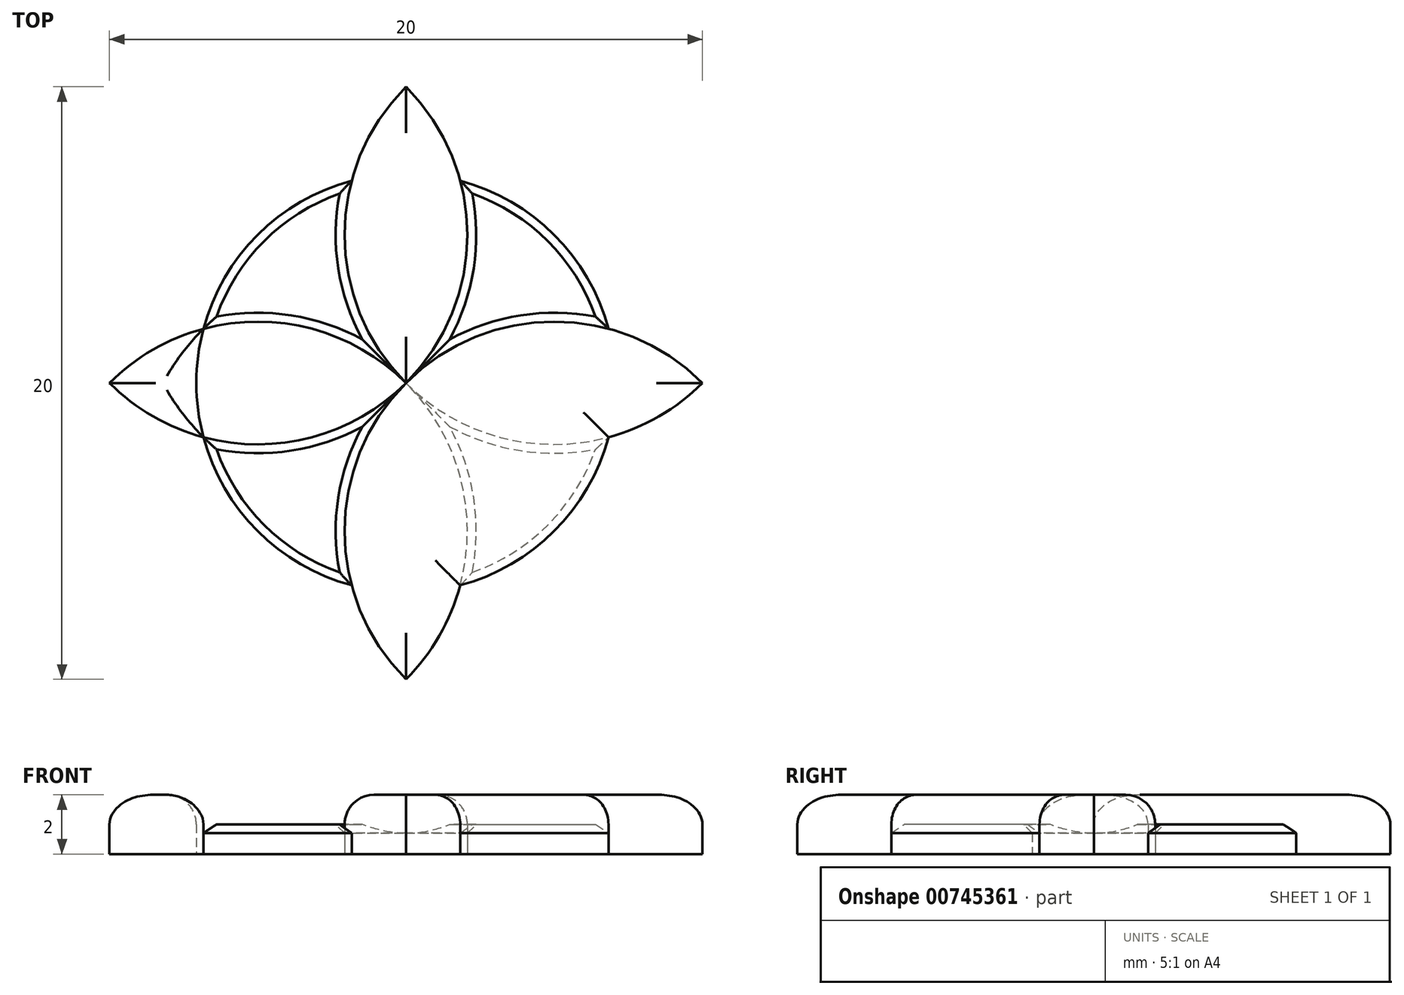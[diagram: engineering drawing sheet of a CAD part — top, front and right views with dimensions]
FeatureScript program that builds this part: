
annotation { "Feature Type Name" : "Feature", "Feature Type Description" : "" }
export const myFeature = defineFeature(function(context is Context, id is Id, definition is map)
    precondition{}
    {
        {
            var Q0;
            Q0=qCreatedBy(makeId("Top.planeOp"),FACE);
            var sketch = newSketch(context, id + "F0", { "sketchPlane" : qUnion([Q0])});
            skPoint(sketch, "E0.middle", {"position": v(0, 0) * mm});
            skArc(sketch, "E1", {"start": v(0, 10) * mm, "mid": v(0, 0) * mm, "end": v(10, 0) * mm});
            skArc(sketch, "E2", {"start": v(10, 0) * mm, "mid": v(0, 0) * mm, "end": v(0, -10) * mm});
            skArc(sketch, "E3", {"start": v(0, -10) * mm, "mid": v(0, 0) * mm, "end": v(-10, 0) * mm});
            skArc(sketch, "E4", {"start": v(-10, 0) * mm, "mid": v(0, 0) * mm, "end": v(0, 10) * mm});
            skCircle(sketch, "E5", {"center": v(0, 0) * mm, "radius": 7.07 * mm});
            skSolve(sketch);
        }
        {
            var Q0;
            {var subQ0=sQuery(id+"F0.wireOp",EDGE,"E5");var subQ1=sQuery(id+"F0.wireOp",EDGE,"E1");var subQ2=makeQuery(id+"F0.imprint","INTERSECT",VERTEX,{"disambiguationData":[OD(0.0)],"derivedFrom":[subQ1,subQ0]});Q0=makeQuery(id+"F0.imprint","IMPRINT",FACE,{"disambiguationData":[TD([[makeQuery(id+"F0.imprint","IMPRINT",EDGE,{"disambiguationData":[TD([[subQ2,1.0]])],"derivedFrom":subQ0}),1.0]])]});}
            var Q1;
            {var subQ0=sQuery(id+"F0.wireOp",EDGE,"E4");var subQ1=sQuery(id+"F0.wireOp",EDGE,"E1");var subQ2=makeQuery(id+"F0.imprint","INTERSECT",VERTEX,{"derivedFrom":[subQ1,subQ0]});Q1=makeQuery(id+"F0.imprint","IMPRINT",FACE,{"disambiguationData":[TD([[makeQuery(id+"F0.imprint","IMPRINT",EDGE,{"disambiguationData":[TD([[subQ2,-1.0]])],"derivedFrom":subQ1}),1.0]])]});}
            var Q2;
            {var subQ0=sQuery(id+"F0.wireOp",EDGE,"E5");var subQ1=sQuery(id+"F0.wireOp",EDGE,"E1");var subQ2=makeQuery(id+"F0.imprint","INTERSECT",VERTEX,{"disambiguationData":[OD(1.0)],"derivedFrom":[subQ1,subQ0]});Q2=makeQuery(id+"F0.imprint","IMPRINT",FACE,{"disambiguationData":[TD([[makeQuery(id+"F0.imprint","IMPRINT",EDGE,{"disambiguationData":[TD([[subQ2,-1.0]])],"derivedFrom":subQ0}),1.0]])]});}
            var Q3;
            {var subQ0=sQuery(id+"F0.wireOp",EDGE,"E2");var subQ1=sQuery(id+"F0.wireOp",EDGE,"E1");var subQ2=makeQuery(id+"F0.imprint","INTERSECT",VERTEX,{"derivedFrom":[subQ1,subQ0]});Q3=makeQuery(id+"F0.imprint","IMPRINT",FACE,{"disambiguationData":[TD([[makeQuery(id+"F0.imprint","IMPRINT",EDGE,{"disambiguationData":[TD([[subQ2,1.0]])],"derivedFrom":subQ1}),1.0]])]});}
            var Q4;
            {var subQ0=sQuery(id+"F0.wireOp",EDGE,"E5");var subQ1=sQuery(id+"F0.wireOp",EDGE,"E2");var subQ2=makeQuery(id+"F0.imprint","INTERSECT",VERTEX,{"disambiguationData":[OD(1.0)],"derivedFrom":[subQ1,subQ0]});Q4=makeQuery(id+"F0.imprint","IMPRINT",FACE,{"disambiguationData":[TD([[makeQuery(id+"F0.imprint","IMPRINT",EDGE,{"disambiguationData":[TD([[subQ2,-1.0]])],"derivedFrom":subQ0}),1.0]])]});}
            var Q5;
            {var subQ0=sQuery(id+"F0.wireOp",EDGE,"E3");var subQ1=sQuery(id+"F0.wireOp",EDGE,"E2");var subQ2=makeQuery(id+"F0.imprint","INTERSECT",VERTEX,{"derivedFrom":[subQ1,subQ0]});Q5=makeQuery(id+"F0.imprint","IMPRINT",FACE,{"disambiguationData":[TD([[makeQuery(id+"F0.imprint","IMPRINT",EDGE,{"disambiguationData":[TD([[subQ2,1.0]])],"derivedFrom":subQ1}),1.0]])]});}
            var Q6;
            {var subQ0=sQuery(id+"F0.wireOp",EDGE,"E5");var subQ1=sQuery(id+"F0.wireOp",EDGE,"E3");var subQ2=makeQuery(id+"F0.imprint","INTERSECT",VERTEX,{"disambiguationData":[OD(1.0)],"derivedFrom":[subQ1,subQ0]});Q6=makeQuery(id+"F0.imprint","IMPRINT",FACE,{"disambiguationData":[TD([[makeQuery(id+"F0.imprint","IMPRINT",EDGE,{"disambiguationData":[TD([[subQ2,-1.0]])],"derivedFrom":subQ0}),1.0]])]});}
            var Q7;
            {var subQ0=sQuery(id+"F0.wireOp",EDGE,"E4");var subQ1=sQuery(id+"F0.wireOp",EDGE,"E3");var subQ2=makeQuery(id+"F0.imprint","INTERSECT",VERTEX,{"derivedFrom":[subQ1,subQ0]});Q7=makeQuery(id+"F0.imprint","IMPRINT",FACE,{"disambiguationData":[TD([[makeQuery(id+"F0.imprint","IMPRINT",EDGE,{"disambiguationData":[TD([[subQ2,1.0]])],"derivedFrom":subQ1}),1.0]])]});}
            extrude(context, id + "F1", {"entities" : qUnion([Q0, Q1, Q2, Q3, Q4, Q5, Q6, Q7]), "depth" : 2 * mm, "offsetDistance" : 25 * mm});
        }
        {
            var Q0;
            {var subQ0=sQuery(id+"F0.wireOp",EDGE,"E5");var subQ1=sQuery(id+"F0.wireOp",EDGE,"E1");var subQ2=makeQuery(id+"F0.imprint","INTERSECT",VERTEX,{"disambiguationData":[OD(0.0)],"derivedFrom":[subQ1,subQ0]});Q0=makeQuery(id+"F0.imprint","IMPRINT",FACE,{"disambiguationData":[TD([[makeQuery(id+"F0.imprint","IMPRINT",EDGE,{"disambiguationData":[TD([[subQ2,-1.0]])],"derivedFrom":subQ0}),1.0]])]});}
            var Q1;
            {var subQ0=sQuery(id+"F0.wireOp",EDGE,"E5");var subQ1=sQuery(id+"F0.wireOp",EDGE,"E2");var subQ2=makeQuery(id+"F0.imprint","INTERSECT",VERTEX,{"disambiguationData":[OD(0.0)],"derivedFrom":[subQ1,subQ0]});Q1=makeQuery(id+"F0.imprint","IMPRINT",FACE,{"disambiguationData":[TD([[makeQuery(id+"F0.imprint","IMPRINT",EDGE,{"disambiguationData":[TD([[subQ2,-1.0]])],"derivedFrom":subQ0}),1.0]])]});}
            var Q2;
            {var subQ0=sQuery(id+"F0.wireOp",EDGE,"E5");var subQ1=sQuery(id+"F0.wireOp",EDGE,"E1");var subQ2=makeQuery(id+"F0.imprint","INTERSECT",VERTEX,{"disambiguationData":[OD(1.0)],"derivedFrom":[subQ1,subQ0]});Q2=makeQuery(id+"F0.imprint","IMPRINT",FACE,{"disambiguationData":[TD([[makeQuery(id+"F0.imprint","IMPRINT",EDGE,{"disambiguationData":[TD([[subQ2,1.0]])],"derivedFrom":subQ0}),1.0]])]});}
            var Q3;
            {var subQ0=sQuery(id+"F0.wireOp",EDGE,"E5");var subQ1=sQuery(id+"F0.wireOp",EDGE,"E2");var subQ2=makeQuery(id+"F0.imprint","INTERSECT",VERTEX,{"disambiguationData":[OD(1.0)],"derivedFrom":[subQ1,subQ0]});Q3=makeQuery(id+"F0.imprint","IMPRINT",FACE,{"disambiguationData":[TD([[makeQuery(id+"F0.imprint","IMPRINT",EDGE,{"disambiguationData":[TD([[subQ2,1.0]])],"derivedFrom":subQ0}),1.0]])]});}
            extrude(context, id + "F2", {"entities" : qUnion([Q0, Q1, Q2, Q3]), "depth" : 1 * mm, "offsetDistance" : 25 * mm});
        }
        {
            var Q0;
            Q0=makeQuery(id+"F1.opExtrude","CAP_FACE",FACE,{"disambiguationData":[OSD([sQuery(id+"F0.wireOp",EDGE,"E1"),sQuery(id+"F0.wireOp",EDGE,"E4")])],"isStart":false});
            var Q1;
            Q1=makeQuery(id+"F1.opExtrude","CAP_FACE",FACE,{"disambiguationData":[OSD([sQuery(id+"F0.wireOp",EDGE,"E1"),sQuery(id+"F0.wireOp",EDGE,"E2")])],"isStart":false});
            var Q2;
            Q2=makeQuery(id+"F1.opExtrude","CAP_FACE",FACE,{"disambiguationData":[OSD([sQuery(id+"F0.wireOp",EDGE,"E2"),sQuery(id+"F0.wireOp",EDGE,"E3")])],"isStart":false});
            var Q3;
            Q3=makeQuery(id+"F1.opExtrude","CAP_FACE",FACE,{"disambiguationData":[OSD([sQuery(id+"F0.wireOp",EDGE,"E3"),sQuery(id+"F0.wireOp",EDGE,"E4")])],"isStart":false});
            fillet(context, id + "F3", {"entities" : qUnion([Q0, Q1, Q2, Q3]), "radius" : 1 * mm, "tangentPropagation" : true, "allowEdgeOverflow" : false});
        }
        {
            var Q0;
            {var subQ0=sQuery(id+"F0.wireOp",EDGE,"E5");var subQ1=sQuery(id+"F0.wireOp",EDGE,"E2");var subQ2=makeQuery(id+"F0.imprint","INTERSECT",VERTEX,{"disambiguationData":[OD(1.0)],"derivedFrom":[subQ1,subQ0]});var subQ3=sQuery(id+"F0.wireOp",EDGE,"E4");var subQ4=makeQuery(id+"F0.imprint","INTERSECT",VERTEX,{"disambiguationData":[OD(0.0)],"derivedFrom":[subQ3,subQ0]});Q0=makeQuery(id+"F2.opExtrude","CAP_FACE",FACE,{"disambiguationData":[OSD([subQ1,subQ3,subQ0]),TDD([makeQuery(id+"F0.imprint","IMPRINT",EDGE,{"disambiguationData":[TD([[subQ2,1.0]])],"derivedFrom":subQ1}),makeQuery(id+"F0.imprint","IMPRINT",EDGE,{"disambiguationData":[TD([[subQ4,-1.0]])],"derivedFrom":subQ3}),makeQuery(id+"F0.imprint","IMPRINT",EDGE,{"disambiguationData":[TD([[subQ2,1.0]])],"derivedFrom":subQ0})])],"isStart":false});}
            var Q1;
            {var subQ0=sQuery(id+"F0.wireOp",EDGE,"E5");var subQ1=sQuery(id+"F0.wireOp",EDGE,"E1");var subQ2=makeQuery(id+"F0.imprint","INTERSECT",VERTEX,{"disambiguationData":[OD(0.0)],"derivedFrom":[subQ1,subQ0]});var subQ3=sQuery(id+"F0.wireOp",EDGE,"E3");var subQ4=makeQuery(id+"F0.imprint","INTERSECT",VERTEX,{"disambiguationData":[OD(1.0)],"derivedFrom":[subQ3,subQ0]});Q1=makeQuery(id+"F2.opExtrude","CAP_FACE",FACE,{"disambiguationData":[OSD([subQ1,subQ3,subQ0]),TDD([makeQuery(id+"F0.imprint","IMPRINT",EDGE,{"disambiguationData":[TD([[subQ2,-1.0]])],"derivedFrom":subQ1}),makeQuery(id+"F0.imprint","IMPRINT",EDGE,{"disambiguationData":[TD([[subQ4,1.0]])],"derivedFrom":subQ3}),makeQuery(id+"F0.imprint","IMPRINT",EDGE,{"disambiguationData":[TD([[subQ2,-1.0]])],"derivedFrom":subQ0})])],"isStart":false});}
            var Q2;
            {var subQ0=sQuery(id+"F0.wireOp",EDGE,"E5");var subQ1=sQuery(id+"F0.wireOp",EDGE,"E2");var subQ2=makeQuery(id+"F0.imprint","INTERSECT",VERTEX,{"disambiguationData":[OD(0.0)],"derivedFrom":[subQ1,subQ0]});var subQ3=sQuery(id+"F0.wireOp",EDGE,"E4");var subQ4=makeQuery(id+"F0.imprint","INTERSECT",VERTEX,{"disambiguationData":[OD(1.0)],"derivedFrom":[subQ3,subQ0]});Q2=makeQuery(id+"F2.opExtrude","CAP_FACE",FACE,{"disambiguationData":[OSD([subQ1,subQ3,subQ0]),TDD([makeQuery(id+"F0.imprint","IMPRINT",EDGE,{"disambiguationData":[TD([[subQ2,-1.0]])],"derivedFrom":subQ1}),makeQuery(id+"F0.imprint","IMPRINT",EDGE,{"disambiguationData":[TD([[subQ4,1.0]])],"derivedFrom":subQ3}),makeQuery(id+"F0.imprint","IMPRINT",EDGE,{"disambiguationData":[TD([[subQ2,-1.0]])],"derivedFrom":subQ0})])],"isStart":false});}
            var Q3;
            {var subQ0=sQuery(id+"F0.wireOp",EDGE,"E5");var subQ1=sQuery(id+"F0.wireOp",EDGE,"E1");var subQ2=makeQuery(id+"F0.imprint","INTERSECT",VERTEX,{"disambiguationData":[OD(1.0)],"derivedFrom":[subQ1,subQ0]});var subQ3=sQuery(id+"F0.wireOp",EDGE,"E3");var subQ4=makeQuery(id+"F0.imprint","INTERSECT",VERTEX,{"disambiguationData":[OD(0.0)],"derivedFrom":[subQ3,subQ0]});Q3=makeQuery(id+"F2.opExtrude","CAP_FACE",FACE,{"disambiguationData":[OSD([subQ1,subQ3,subQ0]),TDD([makeQuery(id+"F0.imprint","IMPRINT",EDGE,{"disambiguationData":[TD([[subQ2,1.0]])],"derivedFrom":subQ1}),makeQuery(id+"F0.imprint","IMPRINT",EDGE,{"disambiguationData":[TD([[subQ4,-1.0]])],"derivedFrom":subQ3}),makeQuery(id+"F0.imprint","IMPRINT",EDGE,{"disambiguationData":[TD([[subQ2,1.0]])],"derivedFrom":subQ0})])],"isStart":false});}
            chamfer(context, id + "F4", {"entities" : qUnion([Q0, Q1, Q2, Q3]), "width" : 0.3 * mm, "tangentPropagation" : true});
        }
    });
